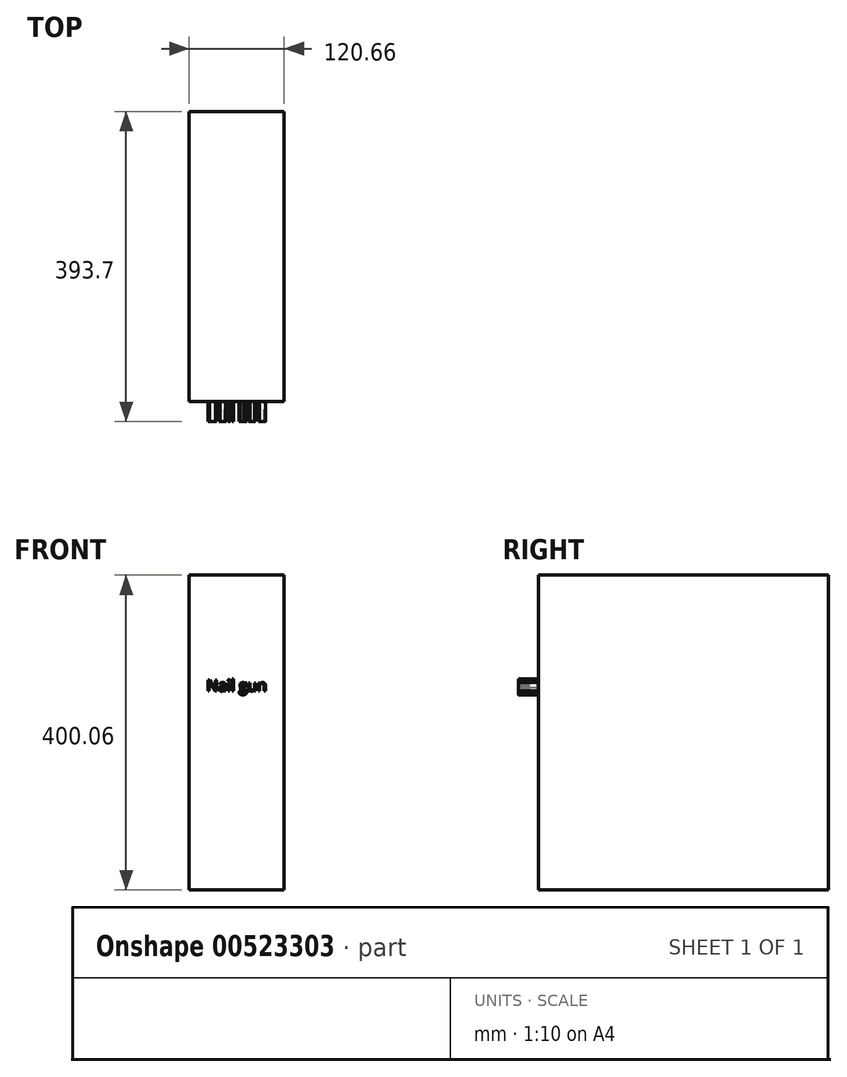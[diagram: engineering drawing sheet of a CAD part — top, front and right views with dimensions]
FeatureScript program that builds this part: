
annotation { "Feature Type Name" : "Feature", "Feature Type Description" : "" }
export const myFeature = defineFeature(function(context is Context, id is Id, definition is map)
    precondition{}
    {
        {
            var Q0;
            Q0=qCreatedBy(makeId("Front.planeOp"),FACE);
            var sketch = newSketch(context, id + "F0", { "sketchPlane" : qUnion([Q0])});
            skLineSegment(sketch, "E0.bottom", {"start": v(60.32, 200.03) * mm, "end": v(-60.33, 200.03) * mm});
            skLineSegment(sketch, "E0.top", {"start": v(60.32, -200.02) * mm, "end": v(-60.33, -200.02) * mm});
            skLineSegment(sketch, "E0.left", {"start": v(60.32, 200.03) * mm, "end": v(60.32, -200.02) * mm});
            skLineSegment(sketch, "E0.right", {"start": v(-60.33, 200.03) * mm, "end": v(-60.33, -200.02) * mm});
            skPoint(sketch, "E0.middle", {"position": v(0, 0) * mm});
            skSolve(sketch);
        }
        {
            var Q0;
            Q0=makeQuery(id+"F0.imprint","IMPRINT",FACE,{"disambiguationData":[TD([[makeQuery(id+"F0.imprint","IMPRINT",EDGE,{"derivedFrom":sQuery(id+"F0.wireOp",EDGE,"E0.bottom")}),1.0]])]});
            extrude(context, id + "F1", {"entities" : qUnion([Q0]), "depth" : 368.3 * mm, "offsetDistance" : 25.4 * mm});
        }
        {
            var Q0;
            Q0=makeQuery(id+"F1.opExtrude","CAP_FACE",FACE,{"disambiguationData":[OSD([sQuery(id+"F0.wireOp",EDGE,"E0.bottom"),sQuery(id+"F0.wireOp",EDGE,"E0.top"),sQuery(id+"F0.wireOp",EDGE,"E0.left"),sQuery(id+"F0.wireOp",EDGE,"E0.right")])],"isStart":false});
            var sketch = newSketch(context, id + "F2", { "sketchPlane" : qUnion([Q0])});
            skText(sketch, "E1", { "text": "Nail gun", "fontName": "OpenSans-Regular.ttf"});
            const initialGuessF2  = {"E1": [-0.03844, 0.05263, 1, 0, 0.0143]};
            skSetInitialGuess(sketch, initialGuessF2);
            skSolve(sketch);
        }
        {
            var Q0;
            Q0 = qSketchRegion(id + "F2", true);
            extrude(context, id + "F3", {"entities" : qUnion([Q0]), "operationType" : NewBodyOperationType.ADD, "depth" : 25.4 * mm, "offsetDistance" : 25.4 * mm});
        }
    });
